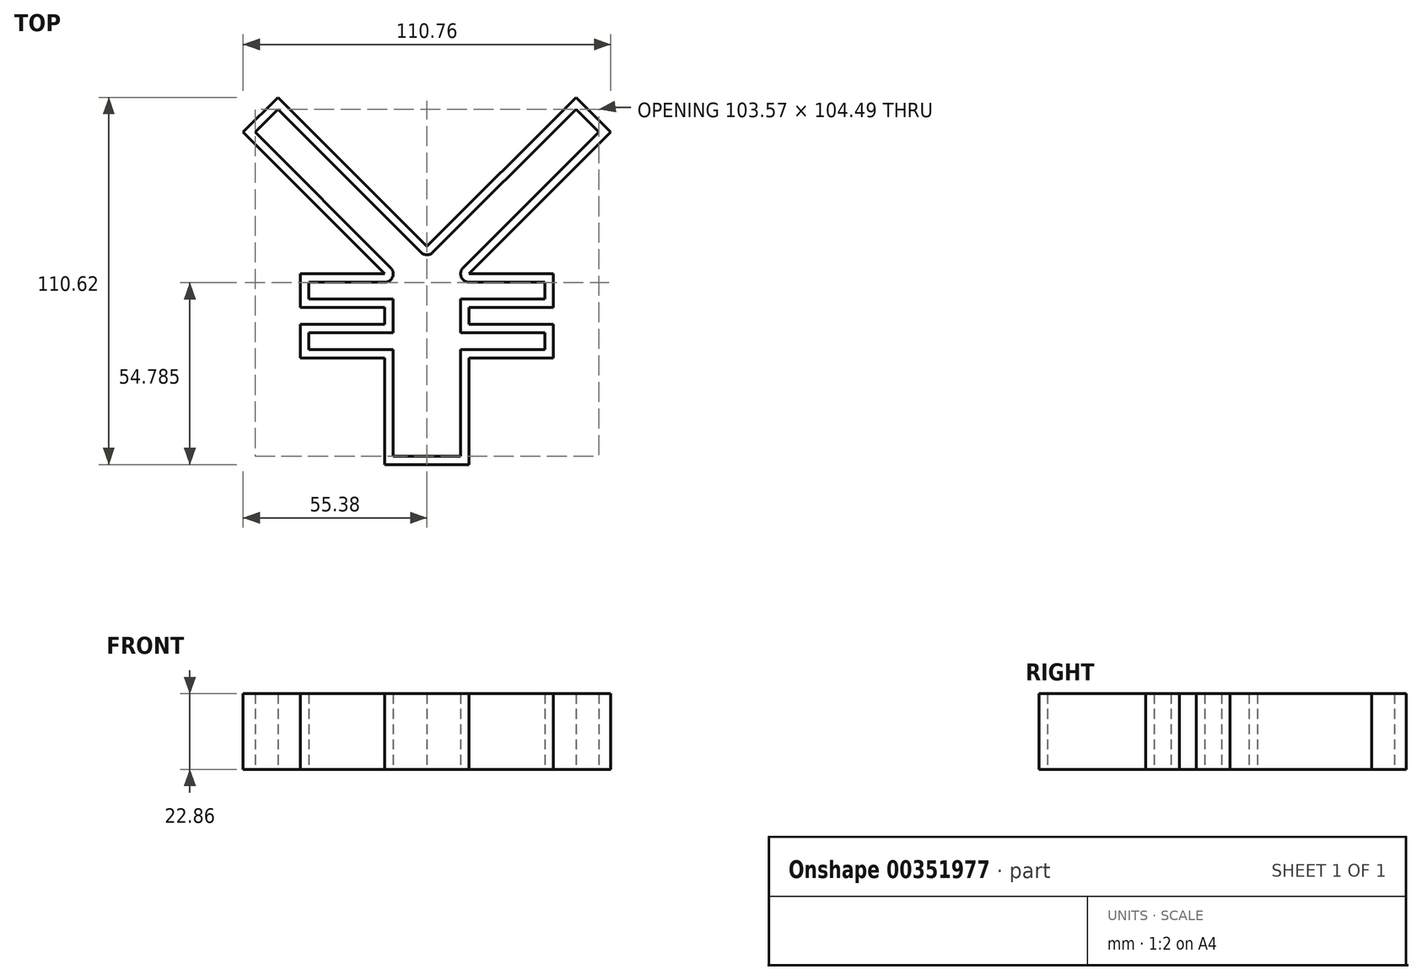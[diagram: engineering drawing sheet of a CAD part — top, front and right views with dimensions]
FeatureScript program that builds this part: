
annotation { "Feature Type Name" : "Feature", "Feature Type Description" : "" }
export const myFeature = defineFeature(function(context is Context, id is Id, definition is map)
    precondition{}
    {
        {
            var Q0;
            Q0=qCreatedBy(makeId("Top.planeOp"),FACE);
            var sketch = newSketch(context, id + "F0", { "sketchPlane" : qUnion([Q0])});
            skLineSegment(sketch, "E0", {"start": v(0, 0) * mm, "end": v(44.9, 44.9) * mm});
            skLineSegment(sketch, "E1", {"start": v(44.9, 44.9) * mm, "end": v(55.38, 34.42) * mm});
            skLineSegment(sketch, "E2", {"start": v(55.38, 34.42) * mm, "end": v(12.7, -8.26) * mm});
            skLineSegment(sketch, "E3", {"start": v(12.7, -8.26) * mm, "end": v(38.1, -8.26) * mm});
            skLineSegment(sketch, "E4", {"start": v(38.1, -8.26) * mm, "end": v(38.1, -18.42) * mm});
            skLineSegment(sketch, "E5", {"start": v(38.1, -18.42) * mm, "end": v(12.7, -18.42) * mm});
            skLineSegment(sketch, "E6", {"start": v(12.7, -18.42) * mm, "end": v(12.7, -23.5) * mm});
            skLineSegment(sketch, "E7", {"start": v(12.7, -23.5) * mm, "end": v(38.1, -23.5) * mm});
            skLineSegment(sketch, "E8", {"start": v(38.1, -23.5) * mm, "end": v(38.1, -33.66) * mm});
            skLineSegment(sketch, "E9", {"start": v(38.1, -33.66) * mm, "end": v(12.7, -33.66) * mm});
            skLineSegment(sketch, "E10", {"start": v(12.7, -33.66) * mm, "end": v(12.7, -65.72) * mm});
            skLineSegment(sketch, "E11", {"start": v(12.7, -65.72) * mm, "end": v(-12.7, -65.72) * mm});
            skLineSegment(sketch, "E12", {"start": v(-12.7, -65.72) * mm, "end": v(-12.7, -33.66) * mm});
            skLineSegment(sketch, "E13", {"start": v(-12.7, -33.66) * mm, "end": v(-38.1, -33.66) * mm});
            skLineSegment(sketch, "E14", {"start": v(-38.1, -33.66) * mm, "end": v(-38.1, -23.5) * mm});
            skLineSegment(sketch, "E15", {"start": v(-38.1, -23.5) * mm, "end": v(-12.7, -23.5) * mm});
            skLineSegment(sketch, "E16", {"start": v(-12.7, -23.5) * mm, "end": v(-12.7, -18.42) * mm});
            skLineSegment(sketch, "E17", {"start": v(-12.7, -18.42) * mm, "end": v(-38.1, -18.42) * mm});
            skLineSegment(sketch, "E18", {"start": v(-38.1, -18.42) * mm, "end": v(-38.1, -8.26) * mm});
            skLineSegment(sketch, "E19", {"start": v(-38.1, -8.26) * mm, "end": v(-12.7, -8.26) * mm});
            skLineSegment(sketch, "E20", {"start": v(-12.7, -8.26) * mm, "end": v(-55.38, 34.42) * mm});
            skLineSegment(sketch, "E21", {"start": v(-55.38, 34.42) * mm, "end": v(-44.9, 44.9) * mm});
            skLineSegment(sketch, "E22", {"start": v(-44.9, 44.9) * mm, "end": v(0, 0) * mm});
            skPoint(sketch, "E23", {"position": v(0, -65.72) * mm});
            skSolve(sketch);
        }
        {
            var Q0;
            Q0 = qSketchRegion(id + "F0", true);
            extrude(context, id + "F1", {"entities" : qUnion([Q0]), "endBound" : BoundingType.SYMMETRIC, "depth" : 25.4 * mm});
        }
        {
            var Q0;
            Q0=makeQuery(id+"F1.opExtrude","CAP_FACE",FACE,{"disambiguationData":[OSD([sQuery(id+"F0.wireOp",EDGE,"E0"),sQuery(id+"F0.wireOp",EDGE,"E1"),sQuery(id+"F0.wireOp",EDGE,"E2"),sQuery(id+"F0.wireOp",EDGE,"E3"),sQuery(id+"F0.wireOp",EDGE,"E4"),sQuery(id+"F0.wireOp",EDGE,"E5"),sQuery(id+"F0.wireOp",EDGE,"E6"),sQuery(id+"F0.wireOp",EDGE,"E7"),sQuery(id+"F0.wireOp",EDGE,"E8"),sQuery(id+"F0.wireOp",EDGE,"E9"),sQuery(id+"F0.wireOp",EDGE,"E10"),sQuery(id+"F0.wireOp",EDGE,"E11"),sQuery(id+"F0.wireOp",EDGE,"E12"),sQuery(id+"F0.wireOp",EDGE,"E13"),sQuery(id+"F0.wireOp",EDGE,"E14"),sQuery(id+"F0.wireOp",EDGE,"E15"),sQuery(id+"F0.wireOp",EDGE,"E16"),sQuery(id+"F0.wireOp",EDGE,"E17"),sQuery(id+"F0.wireOp",EDGE,"E18"),sQuery(id+"F0.wireOp",EDGE,"E19"),sQuery(id+"F0.wireOp",EDGE,"E20"),sQuery(id+"F0.wireOp",EDGE,"E21"),sQuery(id+"F0.wireOp",EDGE,"E22")])],"isStart":false});
            shell(context, id + "F2", {"entities" : qUnion([Q0]), "thickness" : 2.54 * mm});
        }
        {
            var Q0;
            Q0=makeQuery(id+"F1.opExtrude","CAP_FACE",FACE,{"disambiguationData":[OSD([sQuery(id+"F0.wireOp",EDGE,"E0"),sQuery(id+"F0.wireOp",EDGE,"E1"),sQuery(id+"F0.wireOp",EDGE,"E2"),sQuery(id+"F0.wireOp",EDGE,"E3"),sQuery(id+"F0.wireOp",EDGE,"E4"),sQuery(id+"F0.wireOp",EDGE,"E5"),sQuery(id+"F0.wireOp",EDGE,"E6"),sQuery(id+"F0.wireOp",EDGE,"E7"),sQuery(id+"F0.wireOp",EDGE,"E8"),sQuery(id+"F0.wireOp",EDGE,"E9"),sQuery(id+"F0.wireOp",EDGE,"E10"),sQuery(id+"F0.wireOp",EDGE,"E11"),sQuery(id+"F0.wireOp",EDGE,"E12"),sQuery(id+"F0.wireOp",EDGE,"E13"),sQuery(id+"F0.wireOp",EDGE,"E14"),sQuery(id+"F0.wireOp",EDGE,"E15"),sQuery(id+"F0.wireOp",EDGE,"E16"),sQuery(id+"F0.wireOp",EDGE,"E17"),sQuery(id+"F0.wireOp",EDGE,"E18"),sQuery(id+"F0.wireOp",EDGE,"E19"),sQuery(id+"F0.wireOp",EDGE,"E20"),sQuery(id+"F0.wireOp",EDGE,"E21"),sQuery(id+"F0.wireOp",EDGE,"E22")])],"isStart":true});
            extrude(context, id + "F3", {"entities" : qUnion([Q0]), "operationType" : NewBodyOperationType.REMOVE, "oppositeDirection" : true, "depth" : 2.54 * mm});
        }
        {
            var Q0;
            Q0=makeQuery(id+"F2.opShell","OFFSET_EDGE",EDGE,{"disambiguationData":[OSD([sQuery(id+"F0.wireOp",EDGE,"E19"),sQuery(id+"F0.wireOp",EDGE,"E20")])]});
            var Q1;
            Q1=makeQuery(id+"F2.opShell","OFFSET_EDGE",EDGE,{"disambiguationData":[OSD([sQuery(id+"F0.wireOp",EDGE,"E2"),sQuery(id+"F0.wireOp",EDGE,"E3")])]});
            var Q2;
            Q2=makeQuery(id+"F2.opShell","OFFSET_EDGE",EDGE,{"disambiguationData":[OSD([sQuery(id+"F0.wireOp",EDGE,"E0"),sQuery(id+"F0.wireOp",EDGE,"E22")])]});
            fillet(context, id + "F4", {"entities" : qUnion([Q0, Q1, Q2]), "radius" : 2.54 * mm, "tangentPropagation" : true, "allowEdgeOverflow" : false});
        }
    });
